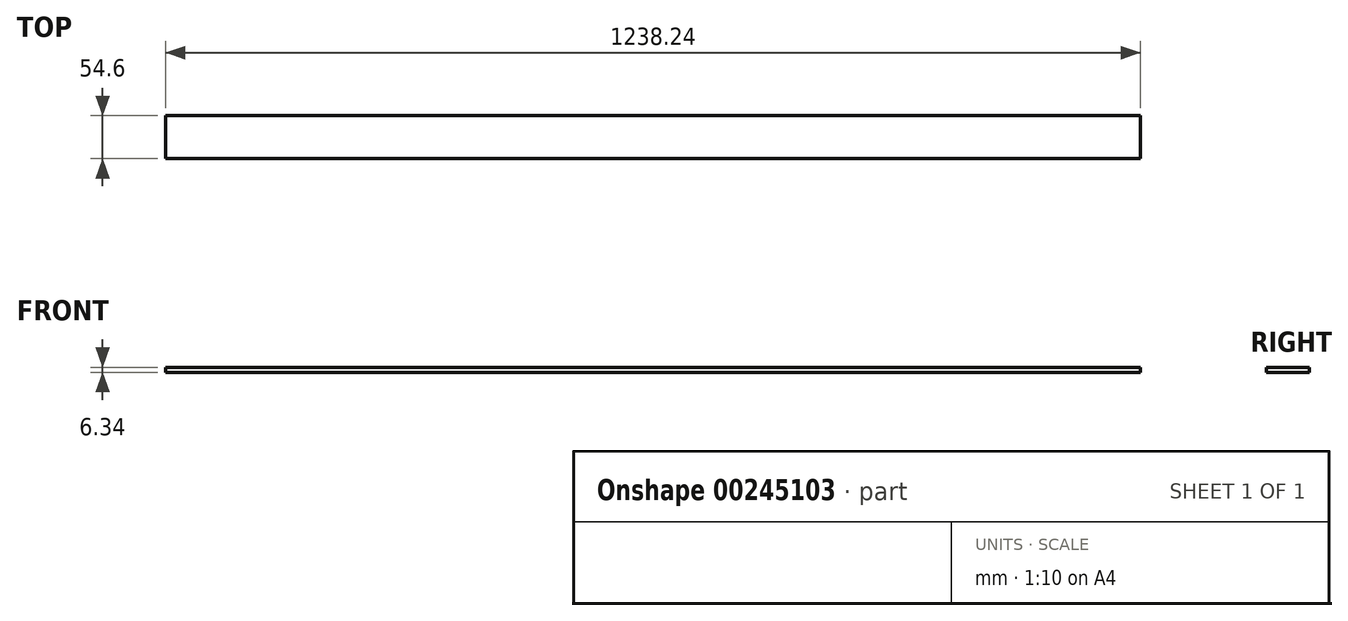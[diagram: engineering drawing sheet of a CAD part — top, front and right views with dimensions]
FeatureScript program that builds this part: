
annotation { "Feature Type Name" : "Feature", "Feature Type Description" : "" }
export const myFeature = defineFeature(function(context is Context, id is Id, definition is map)
    precondition{}
    {
        {
            var Q0;
            Q0=qCreatedBy(makeId("Right.planeOp"),FACE);
            var sketch = newSketch(context, id + "F0", { "sketchPlane" : qUnion([Q0])});
            skLineSegment(sketch, "E0.bottom", {"start": v(27.3, -3.18) * mm, "end": v(-27.3, -3.18) * mm});
            skLineSegment(sketch, "E0.top", {"start": v(27.3, 3.18) * mm, "end": v(-27.3, 3.17) * mm});
            skLineSegment(sketch, "E0.left", {"start": v(27.3, -3.18) * mm, "end": v(27.3, 3.18) * mm});
            skLineSegment(sketch, "E0.right", {"start": v(-27.3, -3.18) * mm, "end": v(-27.3, 3.17) * mm});
            skPoint(sketch, "E0.middle", {"position": v(0, 0) * mm});
            skSolve(sketch);
        }
        {
            var Q0;
            Q0 = qSketchRegion(id + "F0", true);
            extrude(context, id + "F1", {"entities" : qUnion([Q0]), "depth" : 619.12 * mm, "hasSecondDirection" : true, "secondDirectionOppositeDirection" : true, "secondDirectionDepth" : 619.12 * mm});
        }
    });
